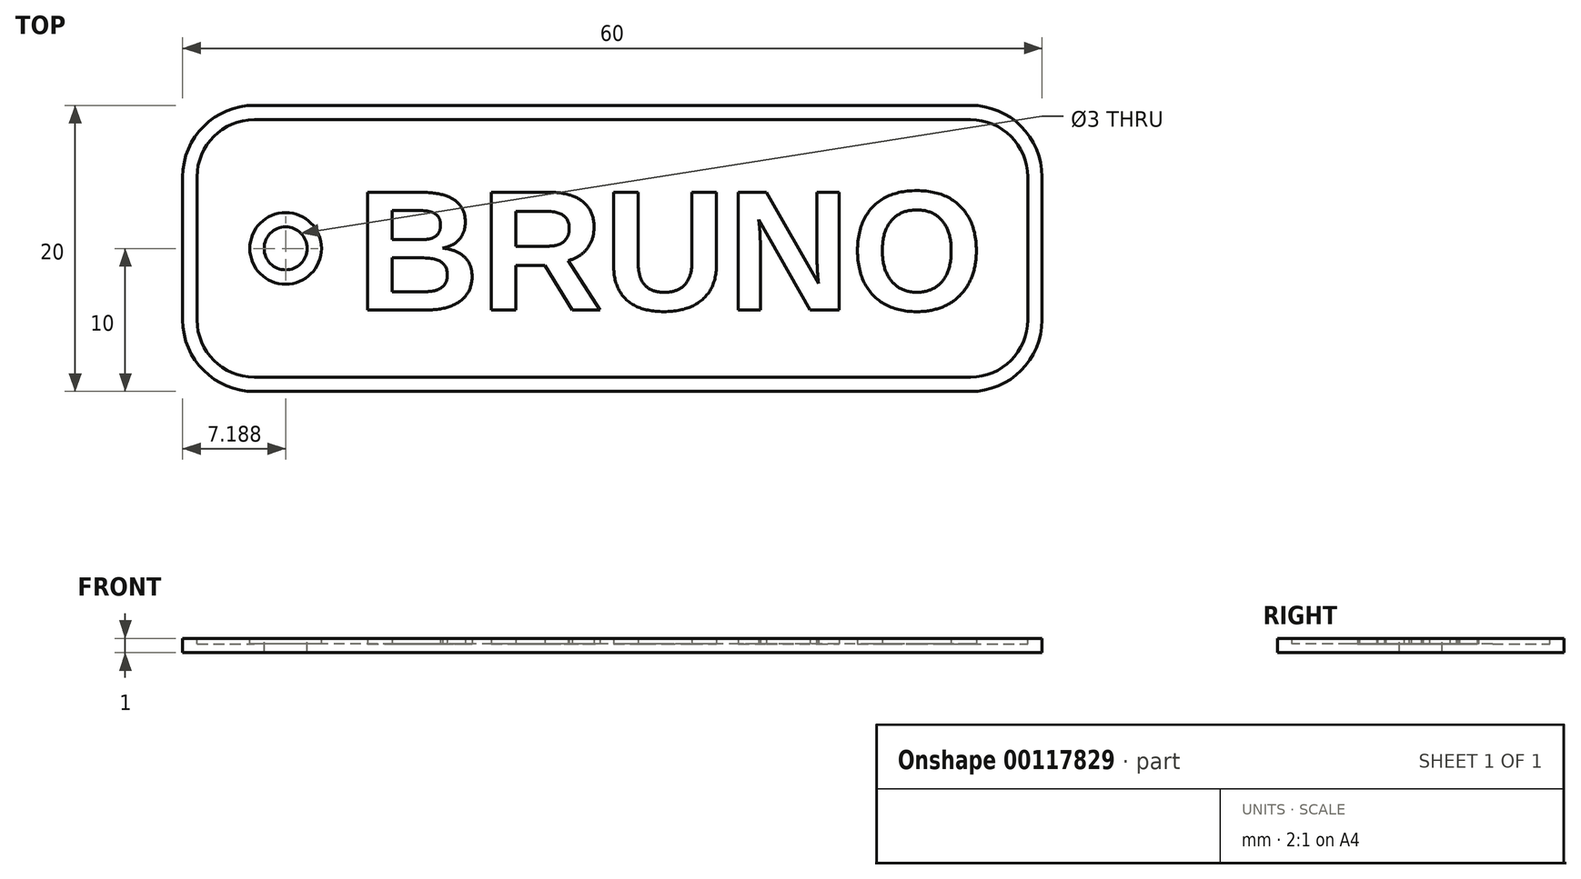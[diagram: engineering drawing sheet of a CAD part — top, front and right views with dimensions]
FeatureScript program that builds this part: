
annotation { "Feature Type Name" : "Feature", "Feature Type Description" : "" }
export const myFeature = defineFeature(function(context is Context, id is Id, definition is map)
    precondition{}
    {
        {
            var Q0;
            Q0=qCreatedBy(makeId("Top.planeOp"),FACE);
            var sketch = newSketch(context, id + "F0", { "sketchPlane" : qUnion([Q0])});
            skLineSegment(sketch, "E0.bottom", {"start": v(30, 10) * mm, "end": v(-30, 10) * mm});
            skLineSegment(sketch, "E0.top", {"start": v(30, -10) * mm, "end": v(-30, -10) * mm});
            skLineSegment(sketch, "E0.left", {"start": v(30, 10) * mm, "end": v(30, -10) * mm});
            skLineSegment(sketch, "E0.right", {"start": v(-30, 10) * mm, "end": v(-30, -10) * mm});
            skPoint(sketch, "E0.middle", {"position": v(0, 0) * mm});
            skSolve(sketch);
        }
        {
            var Q0;
            Q0 = qSketchRegion(id + "F0", true);
            extrude(context, id + "F1", {"entities" : qUnion([Q0]), "depth" : 1 * mm});
        }
        {
            var Q0;
            Q0=makeQuery(id+"F1.opExtrude","SWEPT_EDGE",EDGE,{"disambiguationData":[OSD([sQuery(id+"F0.wireOp",EDGE,"E0.top"),sQuery(id+"F0.wireOp",EDGE,"E0.right")])]});
            var Q1;
            Q1=makeQuery(id+"F1.opExtrude","SWEPT_EDGE",EDGE,{"disambiguationData":[OSD([sQuery(id+"F0.wireOp",EDGE,"E0.top"),sQuery(id+"F0.wireOp",EDGE,"E0.left")])]});
            var Q2;
            Q2=makeQuery(id+"F1.opExtrude","SWEPT_EDGE",EDGE,{"disambiguationData":[OSD([sQuery(id+"F0.wireOp",EDGE,"E0.bottom"),sQuery(id+"F0.wireOp",EDGE,"E0.left")])]});
            var Q3;
            Q3=makeQuery(id+"F1.opExtrude","SWEPT_EDGE",EDGE,{"disambiguationData":[OSD([sQuery(id+"F0.wireOp",EDGE,"E0.bottom"),sQuery(id+"F0.wireOp",EDGE,"E0.right")])]});
            fillet(context, id + "F2", {"entities" : qUnion([Q0, Q1, Q2, Q3]), "radius" : 5 * mm, "tangentPropagation" : true, "allowEdgeOverflow" : false});
        }
        {
            var Q0;
            Q0=makeQuery(id+"F1.opExtrude","CAP_FACE",FACE,{"disambiguationData":[OSD([sQuery(id+"F0.wireOp",EDGE,"E0.bottom"),sQuery(id+"F0.wireOp",EDGE,"E0.top"),sQuery(id+"F0.wireOp",EDGE,"E0.left"),sQuery(id+"F0.wireOp",EDGE,"E0.right")])],"isStart":false});
            var sketch = newSketch(context, id + "F3", { "sketchPlane" : qUnion([Q0])});
            skLineSegment(sketch, "E1.bottom", {"start": v(25, 9) * mm, "end": v(-25, 9) * mm});
            skLineSegment(sketch, "E1.top", {"start": v(25, -9) * mm, "end": v(-25, -9) * mm});
            skLineSegment(sketch, "E1.left", {"start": v(29, 5) * mm, "end": v(29, -5) * mm});
            skLineSegment(sketch, "E1.right", {"start": v(-29, 5) * mm, "end": v(-29, -5) * mm});
            skPoint(sketch, "E1.middle", {"position": v(0, 0) * mm});
            skPoint(sketch, "E2.visualSharp", {"position": v(-29, 9) * mm});
            skArc(sketch, "E2.filletArc", {"start": v(-25, 9) * mm, "mid": v(-27.83, 7.83) * mm, "end": v(-29, 5) * mm});
            skPoint(sketch, "E3.visualSharp", {"position": v(-29, -9) * mm});
            skArc(sketch, "E3.filletArc", {"start": v(-29, -5) * mm, "mid": v(-27.83, -7.83) * mm, "end": v(-25, -9) * mm});
            skPoint(sketch, "E4.visualSharp", {"position": v(29, -9) * mm});
            skArc(sketch, "E4.filletArc", {"start": v(25, -9) * mm, "mid": v(27.83, -7.83) * mm, "end": v(29, -5) * mm});
            skPoint(sketch, "E5.visualSharp", {"position": v(29, 9) * mm});
            skArc(sketch, "E5.filletArc", {"start": v(29, 5) * mm, "mid": v(27.83, 7.83) * mm, "end": v(25, 9) * mm});
            skCircle(sketch, "E6", {"center": v(-22.81, 0) * mm, "radius": 2.5 * mm});
            skSolve(sketch);
        }
        {
            var Q0;
            Q0 = qSketchRegion(id + "F3", true);
            extrude(context, id + "F4", {"entities" : qUnion([Q0]), "operationType" : NewBodyOperationType.REMOVE, "oppositeDirection" : true, "depth" : 0.4 * mm});
        }
        {
            var Q0;
            Q0=makeQuery(id+"F4.boolean.opBoolean","SPLIT",FACE,{"disambiguationData":[TD([makeQuery(id+"F4.opExtrude","SWEPT_FACE",FACE,{"disambiguationData":[OSD([sQuery(id+"F3.wireOp",EDGE,"E6")])]})])],"derivedFrom":makeQuery(id+"F1.opExtrude","CAP_FACE",FACE,{"disambiguationData":[OSD([sQuery(id+"F0.wireOp",EDGE,"E0.bottom"),sQuery(id+"F0.wireOp",EDGE,"E0.top"),sQuery(id+"F0.wireOp",EDGE,"E0.left"),sQuery(id+"F0.wireOp",EDGE,"E0.right")])],"isStart":false})});
            var sketch = newSketch(context, id + "F5", { "sketchPlane" : qUnion([Q0])});
            skCircle(sketch, "E7", {"center": v(-22.81, 0) * mm, "radius": 1.5 * mm});
            skSolve(sketch);
        }
        {
            var Q0;
            Q0 = qSketchRegion(id + "F5", true);
            extrude(context, id + "F6", {"entities" : qUnion([Q0]), "operationType" : NewBodyOperationType.REMOVE, "endBound" : BoundingType.THROUGH_ALL, "oppositeDirection" : true, "depth" : 25 * mm});
        }
        {
            var Q0;
            Q0=makeQuery(id+"F4.boolean.opBoolean","COPY",FACE,{"derivedFrom":makeQuery(id+"F4.opExtrude","CAP_FACE",FACE,{"disambiguationData":[OSD([sQuery(id+"F3.wireOp",EDGE,"E1.bottom"),sQuery(id+"F3.wireOp",EDGE,"E1.top"),sQuery(id+"F3.wireOp",EDGE,"E1.left"),sQuery(id+"F3.wireOp",EDGE,"E1.right"),sQuery(id+"F3.wireOp",EDGE,"E2.filletArc"),sQuery(id+"F3.wireOp",EDGE,"E3.filletArc"),sQuery(id+"F3.wireOp",EDGE,"E4.filletArc"),sQuery(id+"F3.wireOp",EDGE,"E5.filletArc"),sQuery(id+"F3.wireOp",EDGE,"E6")])],"isStart":false})});
            var sketch = newSketch(context, id + "F7", { "sketchPlane" : qUnion([Q0])});
            skText(sketch, "E8", { "text": "BRUNO", "fontName": "Arimo-Bold.ttf"});
            const initialGuessF7  = {"E8": [-0.01788, -0.0043, 1, 0, 0.0086]};
            skSetInitialGuess(sketch, initialGuessF7);
            skSolve(sketch);
        }
        {
            var Q0;
            Q0 = qSketchRegion(id + "F7", true);
            extrude(context, id + "F8", {"entities" : qUnion([Q0]), "operationType" : NewBodyOperationType.ADD, "depth" : 0.4 * mm});
        }
    });
